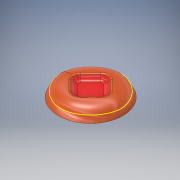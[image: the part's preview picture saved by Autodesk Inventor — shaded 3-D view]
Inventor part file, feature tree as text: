
AUTODESK INVENTOR PART (.ipt)
format: ipt  version: 2018.3 (Build 223284000, 284)  size: 834,560 bytes
history: native  units: in
note: dims shown in document units (in); Inventor stores cm internally (conversion verified against a paired STEP export)
features: other x12, extrude x5, sketch x4, plane x2, split x2, projected_geometry x2, move_body x1, sweep x1, boolean_combine x1, fillet x1
ambient origin geometry x8: Origin, YZ Plane, XZ Plane, XY Plane, X Axis, Y Axis, Z Axis, Center Point
bodies: Solid9 (feature_tree), Solid3 (feature_tree)
feature tree (31):
  other  "Case Bottom Pedestal Fixture.ipt"
  move_body  "Move Body1"
  plane  "Work Plane1"
  split  "Split1"
  other  "Orientation Sketch"
  other  "Contour Fixture Peg Holes"
  other  "Pedestal Peg Holes"
  sweep  "Sweep3"
  split  "Split3"
  extrude  "Extrusion2"  Depth=0.3937in TaperAngle=0.0deg
  boolean_combine  "Combine4"
  fillet  "Fillet7"  Radius=0.7375in
  other  "Pedestal Peg Sketch"
  extrude  "Magnet Holes"  Depth=0.25in
  extrude  "Felt Pads"  Depth=0.375in
  extrude  "Hold-down Pins"  TaperAngle=0.0deg  [1 undecoded]
  extrude  "Mount Bracket"  TaperAngle=0.0deg  [1 undecoded]
  other  "Top Alignment Sketch"
  other  "Vacuum Sketch"
  plane  "Work Plane3"
  other  "CAM Midplane Sketch"
  other  "TaggingFeature1"
  other  "Solid1::Case Bottom Pedestal Fixture.ipt"
  other  "Solid2::Case Bottom Pedestal Fixture.ipt"
  sketch  "Sketch5"  dims[d0=4.5in d1=4.5in]
  sketch  "Sketch8"  dims[d2=0.3937in d3=0.0in d4=0.5625in d5=0.0in d6=0.7375in]
  sketch  "Sketch9"  dims[d7=45.0deg d12=0.25in]
  other  "Peg Sketch"
  sketch  "Sketch15"  dims[d30=4.5in d32=0.125in d58=0.0in d59=0.0in d60=0.0in d61=0.0in d62=0.125in d71=0.5in d72=0.5in d73=0.875in d74=3.1496in d76=360.0deg d78=0.254in d79=3.1496in d81=360.0deg d83=0.375in d84=0.0in d88=0.2in d89=0.0in d101=1.55in d102=1.75in d103=1.0in d104=1.0in d109=0.125in d113=0.256in d114=1.25in d115=1.25in d116=1.5748in d118=360.0deg d120=0.254in d121=1.25in d122=1.25in d123=1.5748in d125=360.0deg d127=0.35in d128=0.0in d129=0.375in d131=0.775in d132=1.5748in d134=360.0deg d136=0.0312in d137=0.0in]
  projected_geometry  "Project Cut Edges2"
  projected_geometry  "Project Cut Edges3"
note: 2 required parameter values undecoded (feature->parameter linkage not recoverable at this tier; creation-order binding heuristic only, values carry confidence <= 0.55)
